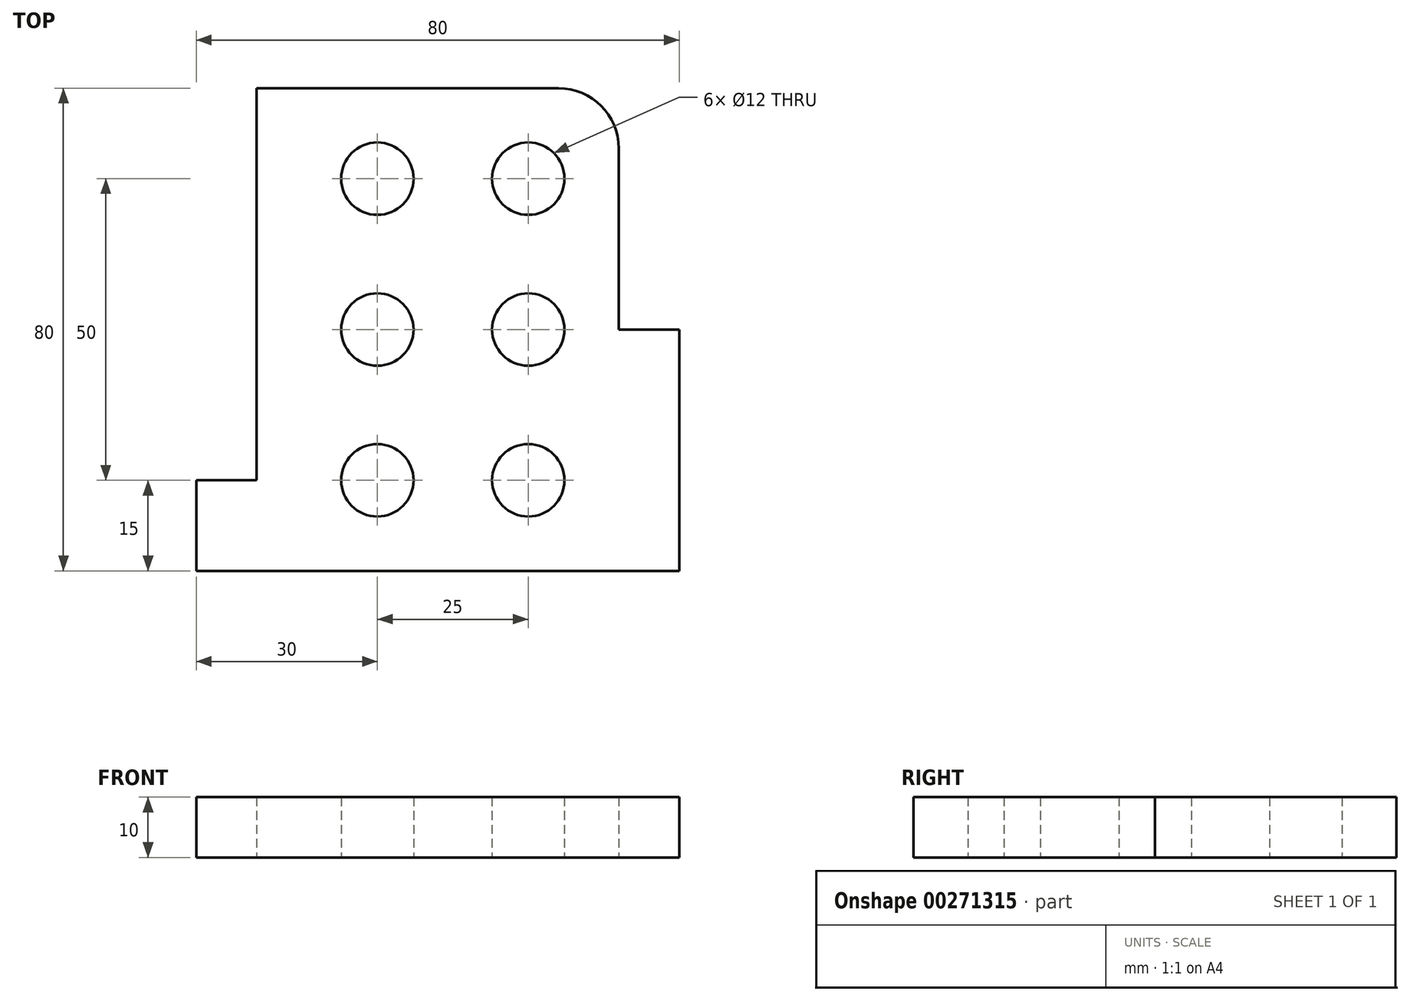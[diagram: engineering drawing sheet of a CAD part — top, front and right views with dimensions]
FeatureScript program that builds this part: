
annotation { "Feature Type Name" : "Feature", "Feature Type Description" : "" }
export const myFeature = defineFeature(function(context is Context, id is Id, definition is map)
    precondition{}
    {
        {
            var Q0;
            Q0=qCreatedBy(makeId("Top.planeOp"),FACE);
            var sketch = newSketch(context, id + "F0", { "sketchPlane" : qUnion([Q0])});
            skLineSegment(sketch, "E0.bottom", {"start": v(0, 0) * mm, "end": v(80, 0) * mm});
            skLineSegment(sketch, "E0.top", {"start": v(10, 80) * mm, "end": v(60, 80) * mm});
            skLineSegment(sketch, "E0.left", {"start": v(0, 0) * mm, "end": v(0, 15) * mm});
            skLineSegment(sketch, "E0.right", {"start": v(80, 0) * mm, "end": v(80, 40) * mm});
            skPoint(sketch, "E1", {"position": v(10, 80) * mm});
            skLineSegment(sketch, "E2", {"start": v(10, 80) * mm, "end": v(10, 15) * mm});
            skLineSegment(sketch, "E3", {"start": v(10, 15) * mm, "end": v(0, 15) * mm});
            skPoint(sketch, "E4", {"position": v(70, 80) * mm});
            skLineSegment(sketch, "E5", {"start": v(70, 70) * mm, "end": v(70, 40) * mm});
            skLineSegment(sketch, "E6", {"start": v(70, 40) * mm, "end": v(80, 40) * mm});
            skPoint(sketch, "E7.orphan", {"position": v(80, 80) * mm});
            skArc(sketch, "E8.filletArc", {"start": v(70, 70) * mm, "mid": v(67.07, 77.07) * mm, "end": v(60, 80) * mm});
            skPoint(sketch, "E9", {"position": v(30, 15) * mm});
            skPoint(sketch, "E10", {"position": v(30, 65) * mm});
            skPoint(sketch, "E11", {"position": v(30, 40) * mm});
            skPoint(sketch, "E12", {"position": v(55, 65) * mm});
            skPoint(sketch, "E13", {"position": v(55, 40) * mm});
            skPoint(sketch, "E14", {"position": v(55, 15) * mm});
            skCircle(sketch, "E15", {"center": v(30, 65) * mm, "radius": 6 * mm});
            skCircle(sketch, "E16", {"center": v(30, 40) * mm, "radius": 6 * mm});
            skCircle(sketch, "E17", {"center": v(30, 15) * mm, "radius": 6 * mm});
            skCircle(sketch, "E18", {"center": v(55, 15) * mm, "radius": 6 * mm});
            skCircle(sketch, "E19", {"center": v(55, 40) * mm, "radius": 6 * mm});
            skCircle(sketch, "E20", {"center": v(55, 65) * mm, "radius": 6 * mm});
            skSolve(sketch);
        }
        {
            var Q0;
            Q0 = qSketchRegion(id + "F0", true);
            extrude(context, id + "F1", {"entities" : qUnion([Q0]), "depth" : 10 * mm});
        }
    });
